# Revit family: IEK_Коннектор_Вертикальный_ГЕРМЕС PLUS
name_source: partatom
category: Обобщенные модели
units: mm (PartAtom-declared; Revit-internal decimal feet)

## family parameters
Всегда вертикально = Да
Может служить основой для арматурных стержней = Нет
На основе рабочей плоскости = Нет
Общий = Нет
При загрузке вырезать с полостями = Нет
Размер круглого соединителя = Использовать диаметр
Тип детали = Нормальный
Точка расчета площади = Нет

## types (1)
- КВ-22
    ADSK_URL страницы изделия = https://www.iek.ru
    ADSK_Версия Revit = 2019
    ADSK_Версия семейства = 1.0
    ADSK_Группирование = III ЭЛЕКТРОУСТАНОВОЧНЫЕ И ЭЛЕКТРОМОНТАЖНЫЕ ИЗДЕЛИЯ
    ADSK_Единица измерения = шт
    ADSK_Завод-изготовитель = IEK
    ADSK_Код изделия = EBMP20-K01
    ADSK_Марка = ГЕРМЕС PLUS
    ADSK_Масса = 0.009
    ADSK_Материал = Цвет белый
    ADSK_Материал наименование = Пластик
    ADSK_Наименование = Коннектор вертикальный КВ-22 ГЕРМЕС PLUS IEK
    IEK_URL = https://www.iek.ru
    IEK_Описание = Изделия серии "ГЕРМЕС PLUS" используются в помещениях с повышенной влажностью или запыленностью, а также под навесом на открытом воздухе.
    IEK_Цена за единицу = 37.66
    KSI_CMa_Строительные материалы = 01.7.14.03
    Изготовитель = IEK
    Совместимость = Серия Гермес Plus
    Тип компонента = Коннектор/соединитель
